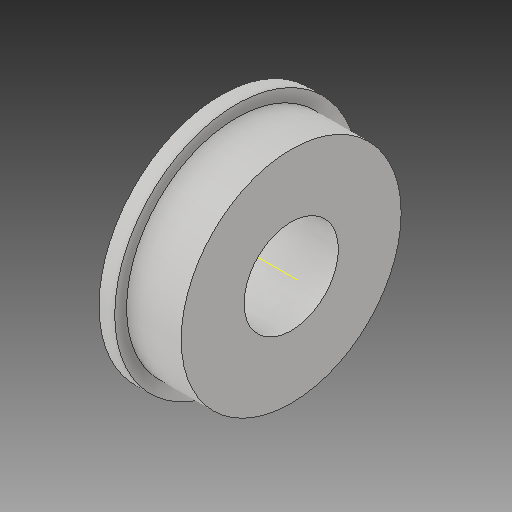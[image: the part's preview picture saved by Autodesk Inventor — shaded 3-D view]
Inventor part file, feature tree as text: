
AUTODESK INVENTOR PART (.ipt)
format: ipt  version: 2019.4 (Build 234330000, 330)  size: 132,608 bytes
history: native  units: in
note: dims shown in document units (in); Inventor stores cm internally (conversion verified against a paired STEP export)
features: revolve x1
ambient origin geometry x8: Origin, YZ Plane, XZ Plane, XY Plane, X Axis, Y Axis, Z Axis, Center Point
bodies: Solid1 (feature_tree)
feature tree (1):
  revolve  "Revolve1"  [1 undecoded]
note: 1 required parameter value undecoded (feature->parameter linkage not recoverable at this tier; creation-order binding heuristic only, values carry confidence <= 0.55)
